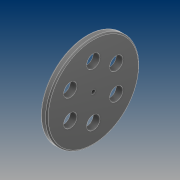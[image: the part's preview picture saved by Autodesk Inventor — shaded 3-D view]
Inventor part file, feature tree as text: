
AUTODESK INVENTOR PART (.ipt)
format: ipt  version: 2021 (Build 250183000, 183)  size: 133,632 bytes
history: native  units: mm
features: extrude x2, sketch x2, fillet x1, pattern_circular x1
ambient origin geometry x8: Origin, YZ Plane, XZ Plane, XY Plane, X Axis, Y Axis, Z Axis, Center Point
bodies: Solid1 (feature_tree)
feature tree (6):
  extrude  "Extrusion1"  Depth=10.0mm
  fillet  "Fillet1"  Radius=10.0mm
  extrude  "Extrusion2"  Depth=10.0mm
  pattern_circular  "Circular Pattern1"  Count=4  [1 undecoded]
  sketch  "Sketch1"  dims[d0=140.0mm d1=6.0mm d2=10.0mm d3=0.0mm]
  sketch  "Sketch2"  dims[d4=2.0mm d5=20.0mm d6=40.0mm d7=10.0mm d8=0.0mm d9=60.0mm d10=360.0deg]
note: 1 required parameter value undecoded (feature->parameter linkage not recoverable at this tier; creation-order binding heuristic only, values carry confidence <= 0.55)
